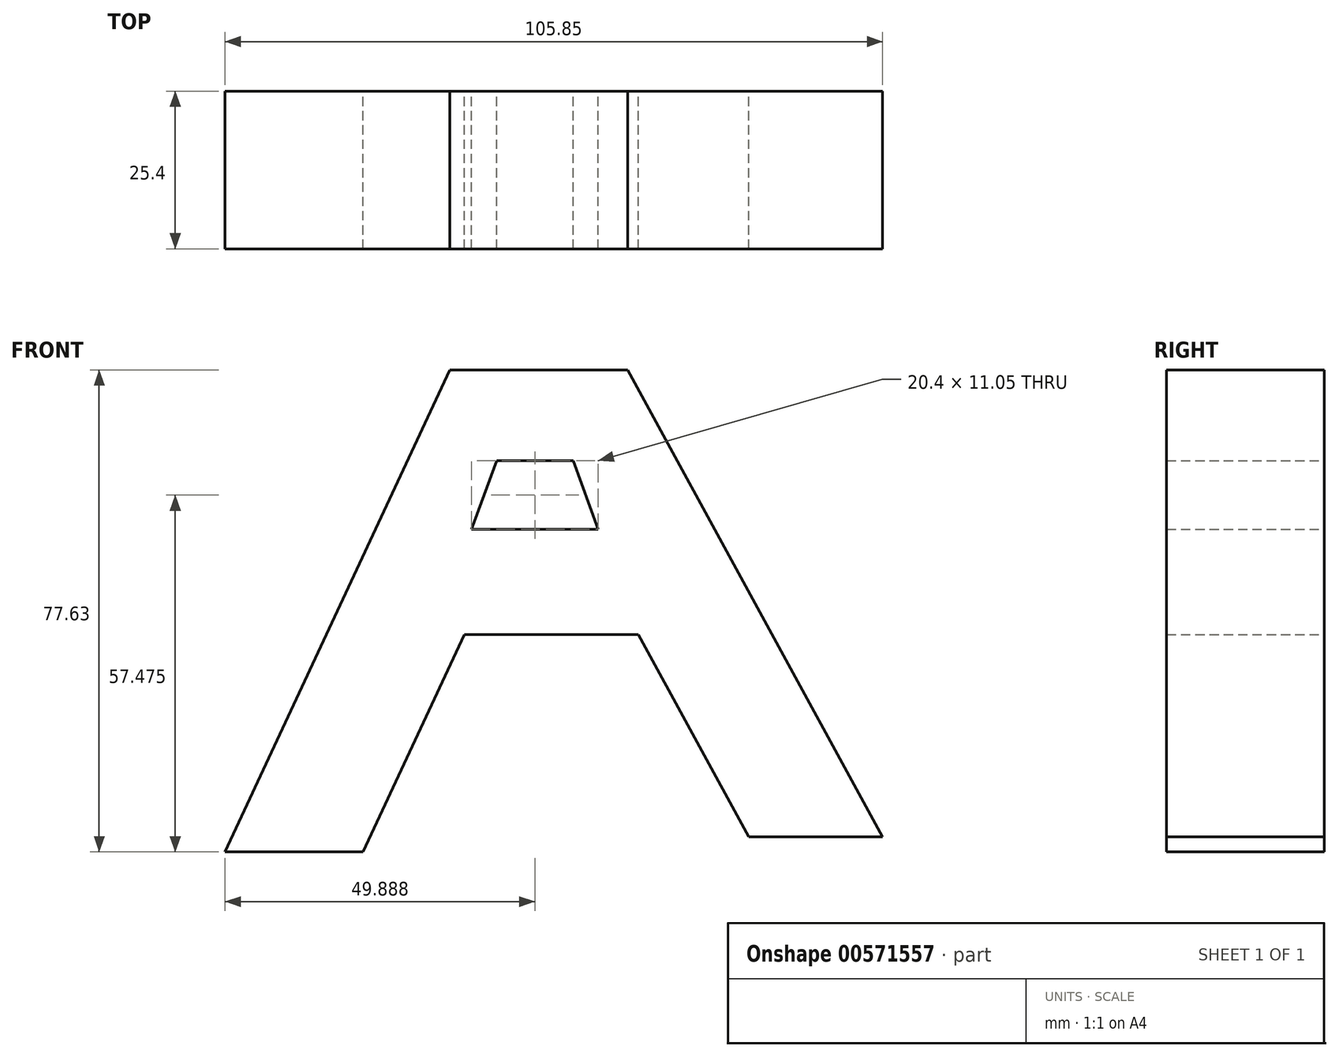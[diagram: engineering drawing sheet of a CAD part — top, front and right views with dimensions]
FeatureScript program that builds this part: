
annotation { "Feature Type Name" : "Feature", "Feature Type Description" : "" }
export const myFeature = defineFeature(function(context is Context, id is Id, definition is map)
    precondition{}
    {
        {
            var Q0;
            Q0=qCreatedBy(makeId("Front.planeOp"),FACE);
            var sketch = newSketch(context, id + "F0", { "sketchPlane" : qUnion([Q0])});
            skLineSegment(sketch, "E0", {"start": v(-47.61, -34.63) * mm, "end": v(-11.41, 43) * mm});
            skLineSegment(sketch, "E1", {"start": v(-11.41, 43) * mm, "end": v(17.24, 43) * mm});
            skLineSegment(sketch, "E2", {"start": v(17.24, 43) * mm, "end": v(58.24, -32.2) * mm});
            skLineSegment(sketch, "E3", {"start": v(-3.9, 28.37) * mm, "end": v(8.46, 28.37) * mm});
            skLineSegment(sketch, "E4", {"start": v(8.46, 28.37) * mm, "end": v(12.48, 17.32) * mm});
            skLineSegment(sketch, "E5", {"start": v(12.48, 17.32) * mm, "end": v(-7.92, 17.32) * mm});
            skLineSegment(sketch, "E6", {"start": v(-7.92, 17.32) * mm, "end": v(-3.9, 28.37) * mm});
            skLineSegment(sketch, "E7", {"start": v(-25.4, -34.63) * mm, "end": v(-9.08, 0.38) * mm});
            skLineSegment(sketch, "E8", {"start": v(-9.08, 0.38) * mm, "end": v(18.92, 0.38) * mm});
            skLineSegment(sketch, "E9", {"start": v(18.92, 0.38) * mm, "end": v(36.69, -32.2) * mm});
            skLineSegment(sketch, "E10", {"start": v(-47.61, -34.63) * mm, "end": v(-25.4, -34.63) * mm});
            skLineSegment(sketch, "E11", {"start": v(36.69, -32.2) * mm, "end": v(58.24, -32.2) * mm});
            skSolve(sketch);
        }
        {
            var Q0;
            Q0 = qSketchRegion(id + "F0", true);
            extrude(context, id + "F1", {"entities" : qUnion([Q0]), "depth" : 25.4 * mm, "offsetDistance" : 25.4 * mm});
        }
    });
